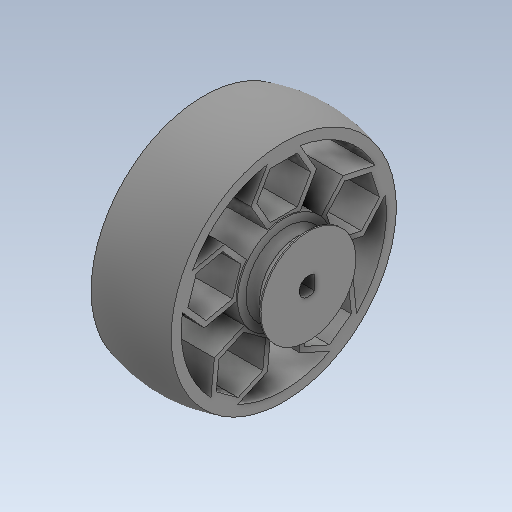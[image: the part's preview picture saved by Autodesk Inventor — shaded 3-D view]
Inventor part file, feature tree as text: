
AUTODESK INVENTOR PART (.ipt)
format: ipt  version: 2020 (Build 240168000, 168)  size: 403,456 bytes
history: native  units: in
note: dims shown in document units (in); Inventor stores cm internally (conversion verified against a paired STEP export)
features: sketch x4, extrude x2, revolve x2, projected_geometry x1
ambient origin geometry x8: Origin, YZ Plane, XZ Plane, XY Plane, X Axis, Y Axis, Z Axis, Center Point
bodies: Solid1 (feature_tree)
feature tree (9):
  extrude  "Extrusion1"  Depth=0.0394in
  sketch  "Sketch3"  dims[d6=0.6063in d7=0.1575in]
  revolve  "Revolution1"  [1 undecoded]
  extrude  "Extrusion2"  Depth=0.1575in
  revolve  "Revolution2"  [1 undecoded]
  sketch  "Sketch1"  dims[d0=0.1181in d1=0.0394in]
  sketch  "Sketch2"  dims[d3=1.437in d4=0.1181in]
  projected_geometry  "Projected Loop1"
  sketch  "Sketch4"  dims[d8=0.0in d9=1.437in d10=0.063in d11=0.0315in d16=0.5118in d17=0.0in d19=360.0deg d20=0.0787in d24=0.0394in d25=90.0deg d26=45.0deg d28=0.0079in d29=1.9685in d31=360.0deg]
note: 2 required parameter values undecoded (feature->parameter linkage not recoverable at this tier; creation-order binding heuristic only, values carry confidence <= 0.55)
